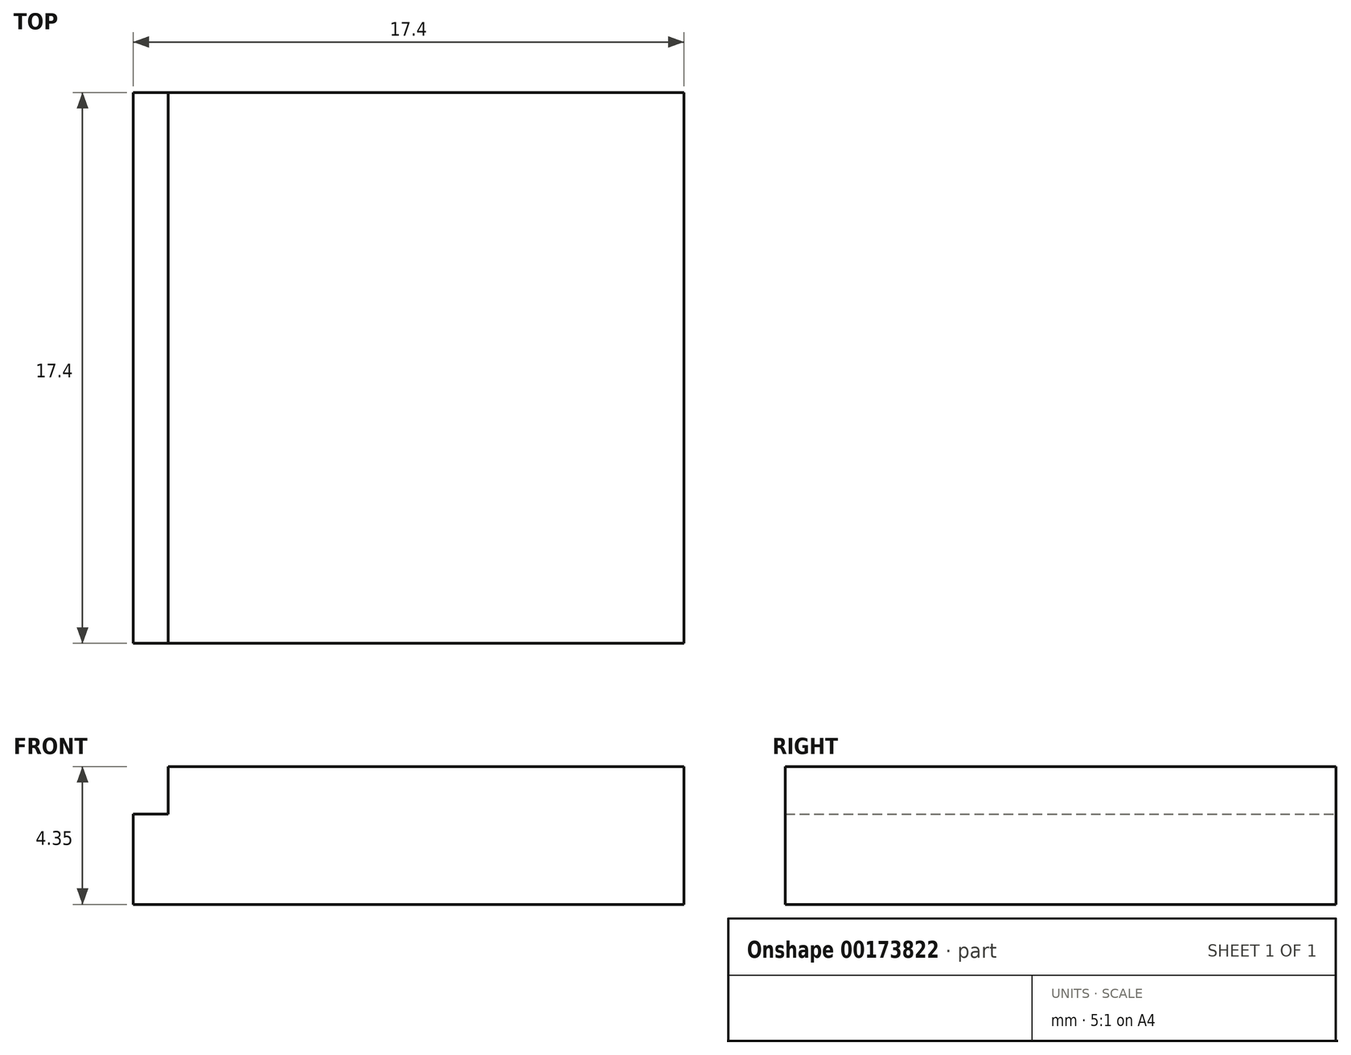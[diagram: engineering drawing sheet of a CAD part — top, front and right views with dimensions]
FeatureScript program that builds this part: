
annotation { "Feature Type Name" : "Feature", "Feature Type Description" : "" }
export const myFeature = defineFeature(function(context is Context, id is Id, definition is map)
    precondition{}
    {
        {
            var Q0;
            Q0=qCreatedBy(makeId("Top.planeOp"),FACE);
            var sketch = newSketch(context, id + "F0", { "sketchPlane" : qUnion([Q0])});
            skLineSegment(sketch, "E0.bottom", {"start": v(0, 0) * mm, "end": v(17.4, 0) * mm});
            skLineSegment(sketch, "E0.top", {"start": v(0, 17.4) * mm, "end": v(17.4, 17.4) * mm});
            skLineSegment(sketch, "E0.left", {"start": v(0, 0) * mm, "end": v(0, 17.4) * mm});
            skLineSegment(sketch, "E0.right", {"start": v(17.4, 0) * mm, "end": v(17.4, 17.4) * mm});
            skSolve(sketch);
        }
        {
            var Q0;
            Q0 = qSketchRegion(id + "F0", true);
            extrude(context, id + "F1", {"entities" : qUnion([Q0]), "depth" : 4.35 * mm, "offsetDistance" : 25 * mm});
        }
        {
            var Q0;
            Q0=makeQuery(id+"F1.opExtrude","CAP_FACE",FACE,{"disambiguationData":[OSD([sQuery(id+"F0.wireOp",EDGE,"E0.bottom"),sQuery(id+"F0.wireOp",EDGE,"E0.top"),sQuery(id+"F0.wireOp",EDGE,"E0.left"),sQuery(id+"F0.wireOp",EDGE,"E0.right")])],"isStart":false});
            var sketch = newSketch(context, id + "F2", { "sketchPlane" : qUnion([Q0])});
            skLineSegment(sketch, "E1.0", {"start": v(0, 0) * mm, "end": v(0, 17.4) * mm});
            skLineSegment(sketch, "E2.0", {"start": v(0, 0) * mm, "end": v(1.1, 0) * mm});
            skLineSegment(sketch, "E3.0", {"start": v(0, 17.4) * mm, "end": v(1.1, 17.4) * mm});
            skLineSegment(sketch, "E4", {"start": v(1.1, 17.4) * mm, "end": v(1.1, 0) * mm});
            skPoint(sketch, "E5.orphan", {"position": v(17.4, 17.4) * mm});
            skPoint(sketch, "E6.orphan", {"position": v(17.4, 0) * mm});
            skSolve(sketch);
        }
        {
            var Q0;
            Q0 = qSketchRegion(id + "F2", true);
            extrude(context, id + "F3", {"entities" : qUnion([Q0]), "operationType" : NewBodyOperationType.REMOVE, "oppositeDirection" : true, "depth" : 1.5 * mm, "offsetDistance" : 25 * mm});
        }
    });
